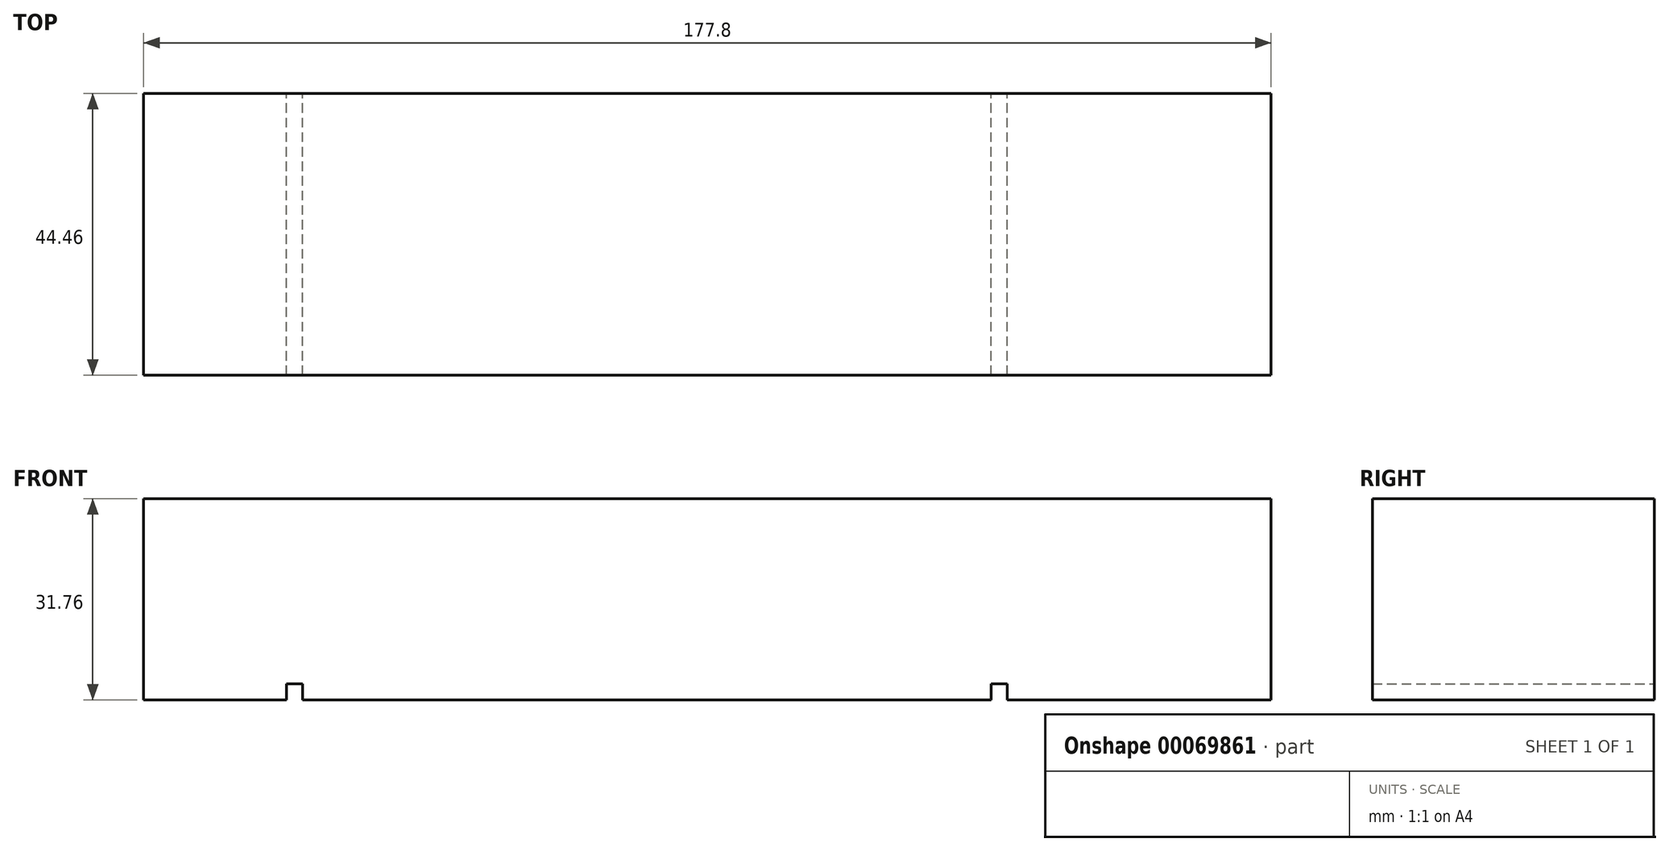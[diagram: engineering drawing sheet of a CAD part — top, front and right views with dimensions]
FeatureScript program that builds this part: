
annotation { "Feature Type Name" : "Feature", "Feature Type Description" : "" }
export const myFeature = defineFeature(function(context is Context, id is Id, definition is map)
    precondition{}
    {
        {
            var Q0;
            Q0=qCreatedBy(makeId("Front.planeOp"),FACE);
            var sketch = newSketch(context, id + "F0", { "sketchPlane" : qUnion([Q0])});
            skLineSegment(sketch, "E0.bottom", {"start": v(-88.9, -15.88) * mm, "end": v(88.9, -15.88) * mm});
            skLineSegment(sketch, "E0.top", {"start": v(-88.9, 15.88) * mm, "end": v(88.9, 15.88) * mm});
            skLineSegment(sketch, "E0.left", {"start": v(-88.9, -15.88) * mm, "end": v(-88.9, 15.88) * mm});
            skLineSegment(sketch, "E0.right", {"start": v(88.9, -15.88) * mm, "end": v(88.9, 15.88) * mm});
            skLineSegment(sketch, "E1", {"start": v(-88.9, 15.88) * mm, "end": v(88.9, -15.88) * mm, "construction": true});
            skPoint(sketch, "E2", {"position": v(0, 0) * mm});
            skSolve(sketch);
        }
        {
            var Q0;
            Q0=makeQuery(id+"F0.imprint","IMPRINT",FACE,{"disambiguationData":[TD([[makeQuery(id+"F0.imprint","IMPRINT",EDGE,{"derivedFrom":sQuery(id+"F0.wireOp",EDGE,"E0.bottom")}),1.0]])]});
            extrude(context, id + "F4", {"entities" : qUnion([Q0]), "endBound" : BoundingType.SYMMETRIC, "depth" : 44.45 * mm});
        }
        {
            var Q0;
            Q0=qCreatedBy(makeId("Front.planeOp"),FACE);
            var sketch = newSketch(context, id + "F1", { "sketchPlane" : qUnion([Q0])});
            skLineSegment(sketch, "E3.0", {"start": v(-88.9, -15.88) * mm, "end": v(88.9, -15.88) * mm, "construction": true});
            skLineSegment(sketch, "E4.bottom", {"start": v(-66.36, -15.88) * mm, "end": v(-63.82, -15.88) * mm});
            skLineSegment(sketch, "E4.top", {"start": v(-66.36, -13.34) * mm, "end": v(-63.82, -13.34) * mm});
            skLineSegment(sketch, "E4.left", {"start": v(-66.36, -15.88) * mm, "end": v(-66.36, -13.34) * mm});
            skLineSegment(sketch, "E4.right", {"start": v(-63.82, -15.88) * mm, "end": v(-63.82, -13.34) * mm});
            skLineSegment(sketch, "E5.bottom", {"start": v(44.77, -15.88) * mm, "end": v(47.3, -15.88) * mm});
            skLineSegment(sketch, "E5.top", {"start": v(44.77, -13.34) * mm, "end": v(47.3, -13.34) * mm});
            skLineSegment(sketch, "E5.left", {"start": v(44.77, -15.88) * mm, "end": v(44.77, -13.34) * mm});
            skLineSegment(sketch, "E5.right", {"start": v(47.3, -15.88) * mm, "end": v(47.3, -13.34) * mm});
            skPoint(sketch, "E6", {"position": v(-65.09, -15.88) * mm});
            skPoint(sketch, "E7", {"position": v(46.04, -15.88) * mm});
            skSolve(sketch);
        }
        {
            var Q0;
            Q0 = qSketchRegion(id + "F1", true);
            extrude(context, id + "F2", {"entities" : qUnion([Q0]), "operationType" : NewBodyOperationType.REMOVE, "endBound" : BoundingType.UP_TO_NEXT, "depth" : 50.8 * mm, "hasSecondDirection" : true, "secondDirectionBound" : SecondDirectionBoundingType.UP_TO_NEXT, "secondDirectionOppositeDirection" : true, "secondDirectionDepth" : 25.4 * mm});
        }
    });
